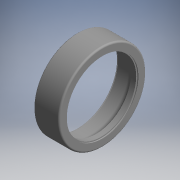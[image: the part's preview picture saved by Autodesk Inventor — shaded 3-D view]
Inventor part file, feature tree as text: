
AUTODESK INVENTOR PART (.ipt)
format: ipt  version: 2017.3 (Build 213256000, 256)  size: 150,016 bytes
history: native  units: mm (DEFAULTED — no unit token found)
features: revolve x1, sketch x1
ambient origin geometry x8: Origin, YZ Plane, XZ Plane, XY Plane, X Axis, Y Axis, Z Axis, Center Point
bodies: Solid1 (feature_tree)
feature tree (2):
  revolve  "Revolution1"  [1 undecoded]
  sketch  "Sketch_4"  dims[d0=360.0deg]
note: 1 required parameter value undecoded (feature->parameter linkage not recoverable at this tier; creation-order binding heuristic only, values carry confidence <= 0.55)
